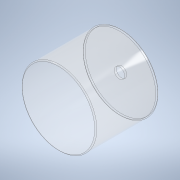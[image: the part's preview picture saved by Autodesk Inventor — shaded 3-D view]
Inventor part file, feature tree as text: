
AUTODESK INVENTOR PART (.ipt)
format: ipt  version: 2020 (Build 240168000, 168)  size: 142,336 bytes
history: native  units: in
note: dims shown in document units (in); Inventor stores cm internally (conversion verified against a paired STEP export)
features: sketch x3, extrude x2, fillet x2, hole x1
ambient origin geometry x8: Origin, YZ Plane, XZ Plane, XY Plane, X Axis, Y Axis, Z Axis, Center Point
bodies: Body1 (feature_tree)
feature tree (8):
  extrude  "Extrusion3"  Depth=2.3622in TaperAngle=0.0deg
  extrude  "Extrusion4"  Depth=0.0394in TaperAngle=0.0deg
  fillet  "Fillet3"  Radius=0.0394in
  fillet  "Fillet4"  Radius=0.0394in
  hole  "Hole4"  [1 undecoded]
  sketch  "Sketch7"  dims[d32=2.7953in d33=2.3622in d34=0.0in]
  sketch  "Sketch9"  dims[d35=2.7165in d36=2.2835in d37=0.0in d38=0.0394in d39=0.0394in]
  sketch  "Sketch10"  dims[d40=0.3937in d41=0.3937in d42=0.2362in d43=0.1575in d44=0.0787in d45=90.0deg d46=0.315in d47=0.8108in]
note: 1 required parameter value undecoded (feature->parameter linkage not recoverable at this tier; creation-order binding heuristic only, values carry confidence <= 0.55)
